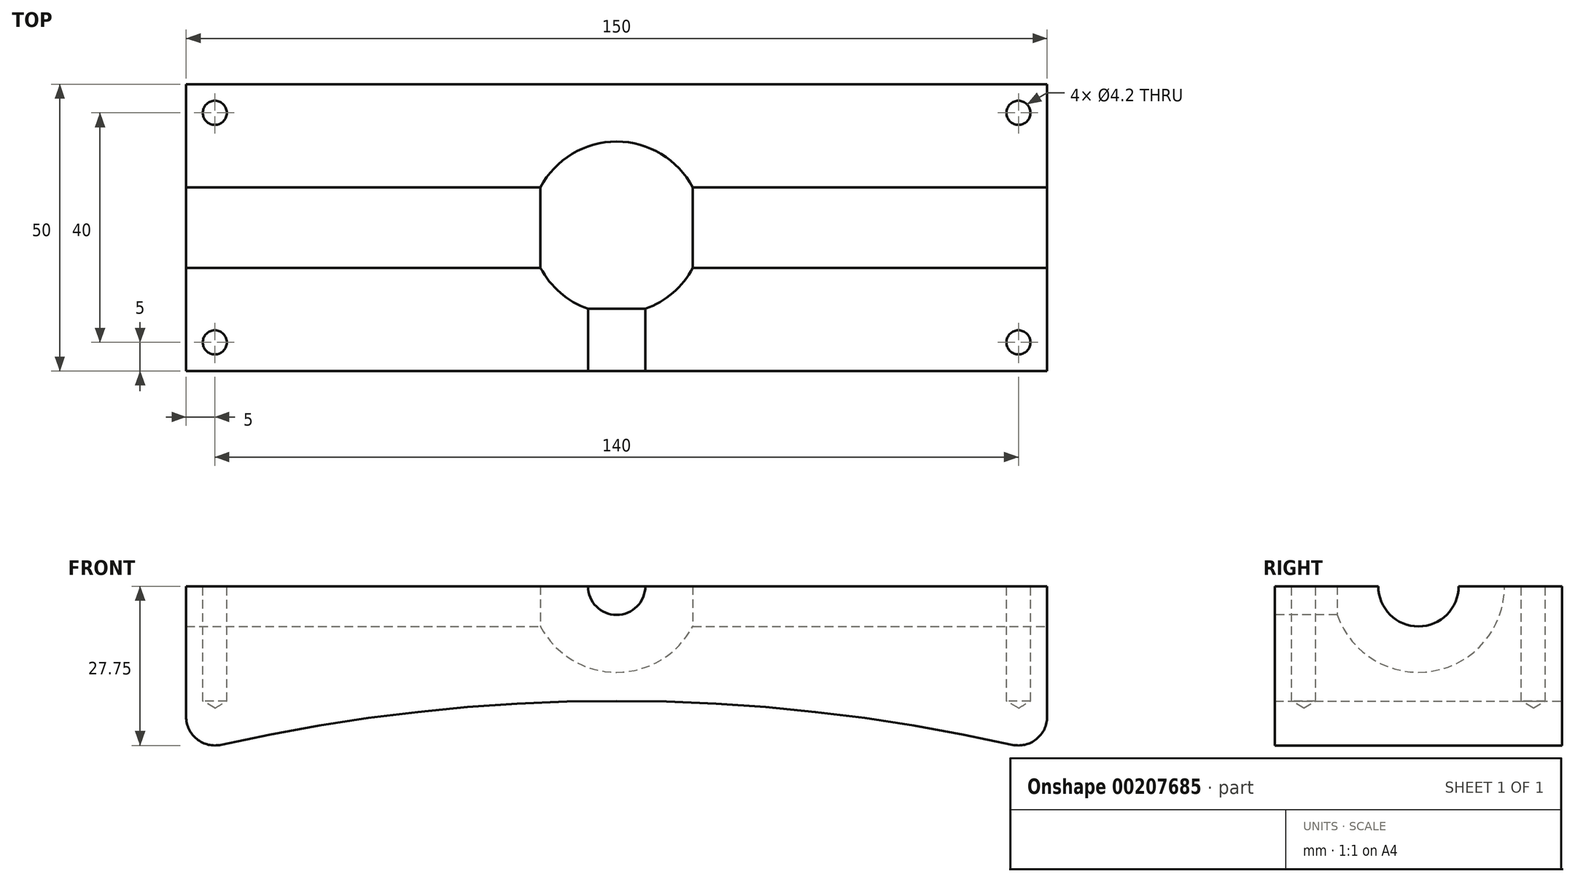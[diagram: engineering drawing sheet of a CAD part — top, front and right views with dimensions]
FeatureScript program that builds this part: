
annotation { "Feature Type Name" : "Feature", "Feature Type Description" : "" }
export const myFeature = defineFeature(function(context is Context, id is Id, definition is map)
    precondition{}
    {
        {
            var Q0;
            Q0=qCreatedBy(makeId("Front.planeOp"),FACE);
            var sketch = newSketch(context, id + "F0", { "sketchPlane" : qUnion([Q0])});
            skCircle(sketch, "E0", {"center": v(0, 0) * mm, "radius": 315 * mm, "construction": true});
            skLineSegment(sketch, "E1", {"start": v(-75, 305.94) * mm, "end": v(0, 0) * mm, "construction": true});
            skLineSegment(sketch, "E2", {"start": v(0, 0) * mm, "end": v(75, 305.94) * mm, "construction": true});
            skArc(sketch, "E3", {"start": v(75, 305.94) * mm, "mid": v(0, 315) * mm, "end": v(-75, 305.94) * mm});
            skLineSegment(sketch, "E4", {"start": v(-75, 335) * mm, "end": v(-75, 305.94) * mm});
            skLineSegment(sketch, "E5", {"start": v(75, 335) * mm, "end": v(75, 305.94) * mm});
            skLineSegment(sketch, "E6", {"start": v(-75, 335) * mm, "end": v(75, 335) * mm});
            skLineSegment(sketch, "E7", {"start": v(0, 335) * mm, "end": v(0, 0) * mm});
            skSolve(sketch);
        }
        {
            var Q0;
            Q0=makeQuery(id+"F0.imprint","IMPRINT",FACE,{"disambiguationData":[TD([[makeQuery(id+"F0.imprint","IMPRINT",EDGE,{"derivedFrom":sQuery(id+"F0.wireOp",EDGE,"E3")}),-1.0]])]});
            extrude(context, id + "F1", {"entities" : qUnion([Q0]), "endBound" : BoundingType.SYMMETRIC, "depth" : 50 * mm});
        }
        {
            var Q0;
            Q0=makeQuery(id+"F1.opExtrude","SWEPT_FACE",FACE,{"disambiguationData":[OSD([sQuery(id+"F0.wireOp",EDGE,"E6")])]});
            var sketch = newSketch(context, id + "F2", { "sketchPlane" : qUnion([Q0])});
            skLineSegment(sketch, "E8", {"start": v(-75, 0) * mm, "end": v(75, 0) * mm, "construction": true});
            skLineSegment(sketch, "E9.bottom", {"start": v(-75, 7) * mm, "end": v(-13.27, 7) * mm});
            skLineSegment(sketch, "E9.top", {"start": v(-75, 0) * mm, "end": v(-13.27, 0) * mm});
            skLineSegment(sketch, "E9.left", {"start": v(-75, 7) * mm, "end": v(-75, 0) * mm});
            skLineSegment(sketch, "E9.right", {"start": v(-13.27, 7) * mm, "end": v(-13.27, 0) * mm, "construction": true});
            skArc(sketch, "E10", {"start": v(15, 0) * mm, "mid": v(0, 15) * mm, "end": v(-15, 0) * mm});
            skLineSegment(sketch, "E11.bottom", {"start": v(13.27, 7) * mm, "end": v(75, 7) * mm});
            skLineSegment(sketch, "E11.top", {"start": v(13.27, 0) * mm, "end": v(75, 0) * mm});
            skLineSegment(sketch, "E11.left", {"start": v(13.27, 7) * mm, "end": v(13.27, 0) * mm, "construction": true});
            skLineSegment(sketch, "E11.right", {"start": v(75, 7) * mm, "end": v(75, 0) * mm});
            skLineSegment(sketch, "E12", {"start": v(-15, 0) * mm, "end": v(15, 0) * mm});
            skSolve(sketch);
        }
        {
            var Q0;
            {var subQ0=sQuery(id+"F2.wireOp",EDGE,"E9.bottom");Q0=makeQuery(id+"F2.imprint","IMPRINT",FACE,{"disambiguationData":[TD([[makeQuery(id+"F2.imprint","IMPRINT",EDGE,{"derivedFrom":subQ0}),-1.0]])]});}
            var Q1;
            {var subQ2=sQuery(id+"F2.wireOp",EDGE,"E12");var subQ4=makeQuery(id+"F2.imprint","IMPRINT",VERTEX,{"disambiguationData":[OD(0.0)],"derivedFrom":subQ2});Q1=makeQuery(id+"F2.imprint","IMPRINT",FACE,{"disambiguationData":[TD([[makeQuery(id+"F2.imprint","IMPRINT",EDGE,{"disambiguationData":[TD([[subQ4,-1.0]])],"derivedFrom":subQ2}),1.0]])]});}
            var Q2;
            {var subQ2=sQuery(id+"F2.wireOp",EDGE,"E11.bottom");Q2=makeQuery(id+"F2.imprint","IMPRINT",FACE,{"disambiguationData":[TD([[makeQuery(id+"F2.imprint","IMPRINT",EDGE,{"derivedFrom":subQ2}),-1.0]])]});}
            var Q3;
            Q3=sQuery(id+"F2.wireOp",EDGE,"E9.top");
            revolve(context, id + "F3", {"operationType" : NewBodyOperationType.REMOVE, "entities" : qUnion([Q0, Q1, Q2]), "axis" : qUnion([Q3]), "revolveType" : RevolveType.FULL, "oppositeDirection" : true});
        }
        {
            var Q0;
            {var subQ0=sQuery(id+"F0.wireOp",EDGE,"E5");var subQ1=sQuery(id+"F0.wireOp",EDGE,"E6");var subQ2=sQuery(id+"F0.wireOp",EDGE,"E4");Q0=makeQuery(id+"F3.boolean.opBoolean","SPLIT",FACE,{"disambiguationData":[TD([makeQuery(id+"F1.opExtrude","CAP_FACE",FACE,{"disambiguationData":[OSD([sQuery(id+"F0.wireOp",EDGE,"E3"),subQ2,subQ0,subQ1])],"isStart":true})])],"derivedFrom":makeQuery(id+"F1.opExtrude","SWEPT_FACE",FACE,{"disambiguationData":[OSD([subQ1])]})});}
            var sketch = newSketch(context, id + "F4", { "sketchPlane" : qUnion([Q0])});
            skCircle(sketch, "E13", {"center": v(-70, 20) * mm, "radius": 5 * mm});
            skCircle(sketch, "E14", {"center": v(-70, -20) * mm, "radius": 5 * mm});
            skCircle(sketch, "E15", {"center": v(70, -20) * mm, "radius": 5 * mm});
            skCircle(sketch, "E16", {"center": v(70, 20) * mm, "radius": 5 * mm});
            skSolve(sketch);
        }
        {
            var Q0;
            Q0=sQuery(id+"F4.wireOp",VERTEX,"E13.center");
            var Q1;
            Q1=sQuery(id+"F4.wireOp",VERTEX,"E14.center");
            var Q2;
            Q2=sQuery(id+"F4.wireOp",VERTEX,"E16.center");
            var Q3;
            Q3=sQuery(id+"F4.wireOp",VERTEX,"E15.center");
            var Q4;
            Q4=makeQuery(id+"F1.opExtrude","SWEPT_BODY",BODY,{"disambiguationData":[OSD([sQuery(id+"F0.wireOp",EDGE,"E3"),sQuery(id+"F0.wireOp",EDGE,"E4"),sQuery(id+"F0.wireOp",EDGE,"E5"),sQuery(id+"F0.wireOp",EDGE,"E6")])]});
            hole(context, id + "F5", {"style" : HoleStyle.SIMPLE, "endStyle" : HoleEndStyle.BLIND, "standardTappedOrClearance" : lookupTablePath({ "standard" : "ISO", "engagement" : "75%", "pitch" : "0.8 mm", "size" : "M5", "type" : "Tapped" }), "standardBlindInLast" : lookupTablePath({ "standard" : "ISO", "engagement" : "75%", "pitch" : "0.8 mm", "size" : "M5", "type" : "Tapped" }), "holeDiameter" : 4.2 * mm, "showTappedDepth" : true, "holeDepth" : 20 * mm, "tappedDepth" : 17.6 * mm, "tapClearance" : 3, "locations" : qUnion([Q0, Q1, Q2, Q3]), "scope" : qUnion([Q4]), "majorDiameter" : 5 * mm});
        }
        {
            var Q0;
            Q0=makeQuery(id+"F1.opExtrude","SWEPT_EDGE",EDGE,{"disambiguationData":[OSD([sQuery(id+"F0.wireOp",EDGE,"E3"),sQuery(id+"F0.wireOp",EDGE,"E4")])]});
            var Q1;
            Q1=makeQuery(id+"F1.opExtrude","SWEPT_EDGE",EDGE,{"disambiguationData":[OSD([sQuery(id+"F0.wireOp",EDGE,"E3"),sQuery(id+"F0.wireOp",EDGE,"E5")])]});
            fillet(context, id + "F6", {"entities" : qUnion([Q0, Q1]), "radius" : 5 * mm, "tangentPropagation" : true, "allowEdgeOverflow" : false});
        }
        {
            var Q0;
            {var subQ0=sQuery(id+"F0.wireOp",EDGE,"E5");var subQ1=sQuery(id+"F0.wireOp",EDGE,"E4");var subQ2=sQuery(id+"F0.wireOp",EDGE,"E6");Q0=makeQuery(id+"F3.boolean.opBoolean","SPLIT",FACE,{"disambiguationData":[TD([makeQuery(id+"F1.opExtrude","CAP_FACE",FACE,{"disambiguationData":[OSD([sQuery(id+"F0.wireOp",EDGE,"E3"),subQ1,subQ0,subQ2])],"isStart":false})])],"derivedFrom":makeQuery(id+"F1.opExtrude","SWEPT_FACE",FACE,{"disambiguationData":[OSD([subQ2])]})});}
            var sketch = newSketch(context, id + "F7", { "sketchPlane" : qUnion([Q0])});
            skLineSegment(sketch, "E17.bottom", {"start": v(-5, 0) * mm, "end": v(0, 0) * mm});
            skLineSegment(sketch, "E17.top", {"start": v(-5, -25) * mm, "end": v(0, -25) * mm});
            skLineSegment(sketch, "E17.left", {"start": v(-5, 0) * mm, "end": v(-5, -25) * mm});
            skLineSegment(sketch, "E17.right", {"start": v(0, 0) * mm, "end": v(0, -25) * mm});
            skSolve(sketch);
        }
        {
            var Q0;
            {var subQ0=sQuery(id+"F7.wireOp",EDGE,"E17.bottom");Q0=makeQuery(id+"F7.imprint","IMPRINT",FACE,{"disambiguationData":[TD([[makeQuery(id+"F7.imprint","IMPRINT",EDGE,{"derivedFrom":subQ0}),-1.0]])]});}
            var Q1;
            {var subQ0=sQuery(id+"F7.wireOp",EDGE,"E17.top");Q1=makeQuery(id+"F7.imprint","IMPRINT",FACE,{"disambiguationData":[TD([[makeQuery(id+"F7.imprint","IMPRINT",EDGE,{"derivedFrom":subQ0}),1.0]])]});}
            var Q2;
            Q2=sQuery(id+"F7.wireOp",EDGE,"E17.right");
            revolve(context, id + "F8", {"operationType" : NewBodyOperationType.REMOVE, "entities" : qUnion([Q0, Q1]), "axis" : qUnion([Q2]), "revolveType" : RevolveType.FULL, "oppositeDirection" : true});
        }
    });
